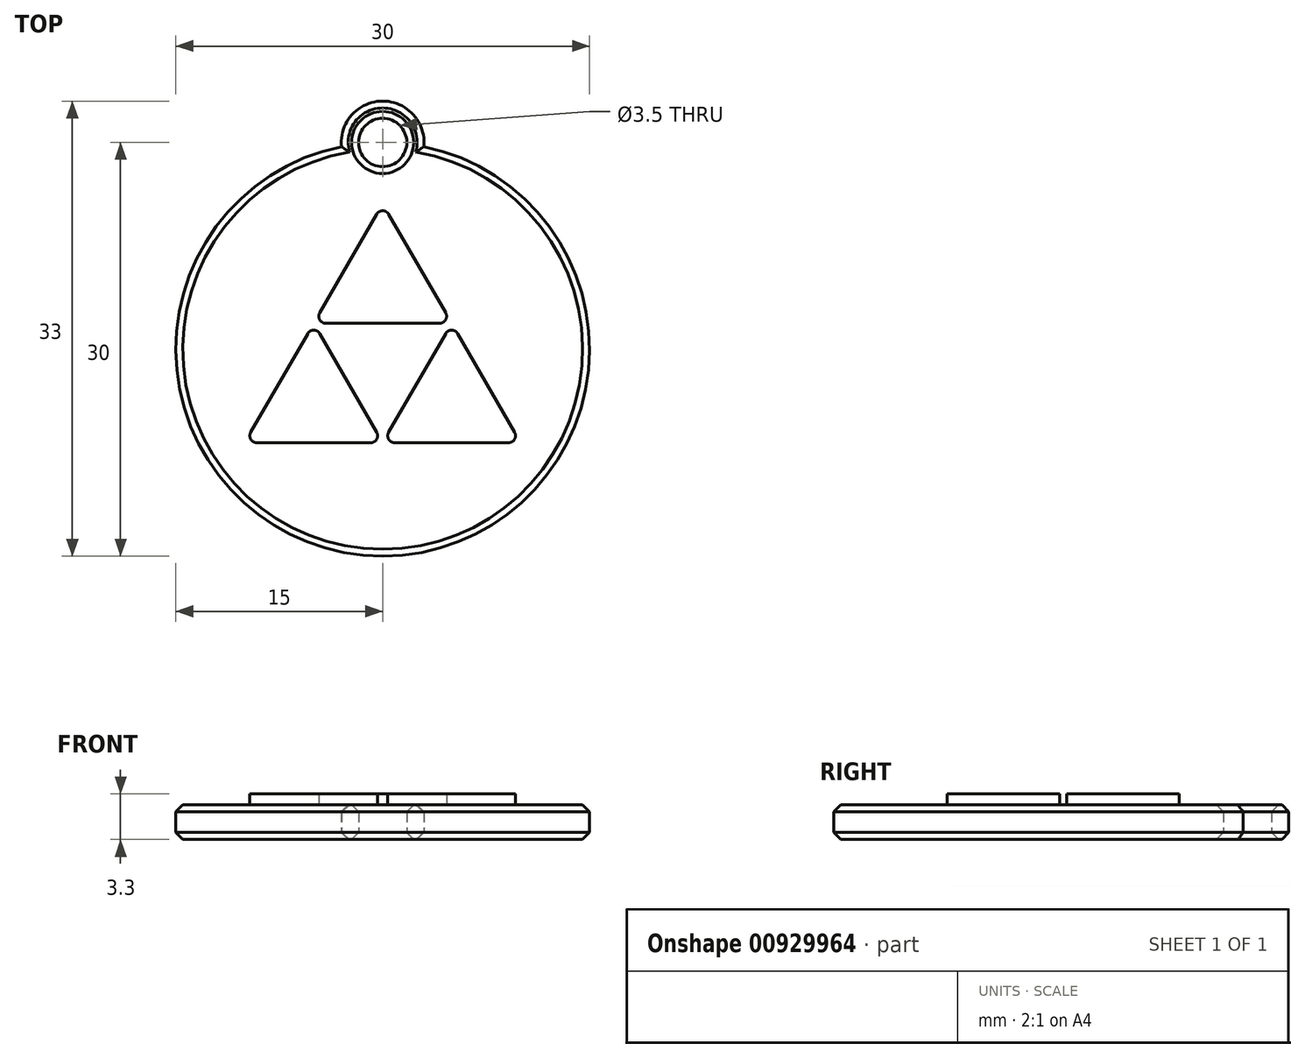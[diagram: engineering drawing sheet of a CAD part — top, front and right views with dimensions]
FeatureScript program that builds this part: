
annotation { "Feature Type Name" : "Feature", "Feature Type Description" : "" }
export const myFeature = defineFeature(function(context is Context, id is Id, definition is map)
    precondition{}
    {
        {
            var Q0;
            Q0=qCreatedBy(makeId("Top.planeOp"),FACE);
            var sketch = newSketch(context, id + "F0", { "sketchPlane" : qUnion([Q0])});
            skArc(sketch, "E0", {"start": v(-2.98, 14.7) * mm, "mid": v(0, -15) * mm, "end": v(2.98, 14.7) * mm});
            skArc(sketch, "E1", {"start": v(2.98, 14.7) * mm, "mid": v(0, 18) * mm, "end": v(-2.98, 14.7) * mm});
            skCircle(sketch, "E2", {"center": v(0, 15) * mm, "radius": 1.75 * mm});
            skSolve(sketch);
        }
        {
            var Q0;
            Q0=makeQuery(id+"F0.imprint","IMPRINT",FACE,{"disambiguationData":[TD([[makeQuery(id+"F0.imprint","IMPRINT",EDGE,{"derivedFrom":sQuery(id+"F0.wireOp",EDGE,"E0")}),1.0]])]});
            extrude(context, id + "F1", {"entities" : qUnion([Q0]), "depth" : 2.5 * mm, "offsetDistance" : 25 * mm});
        }
        {
            var Q0;
            Q0=makeQuery(id+"F1.opExtrude","CAP_FACE",FACE,{"disambiguationData":[OSD([sQuery(id+"F0.wireOp",EDGE,"E0"),sQuery(id+"F0.wireOp",EDGE,"E1"),sQuery(id+"F0.wireOp",EDGE,"E2")])],"isStart":false});
            var sketch = newSketch(context, id + "F2", { "sketchPlane" : qUnion([Q0])});
            skLineSegment(sketch, "E3", {"start": v(4.13, 1.89) * mm, "end": v(-4.13, 1.89) * mm});
            skLineSegment(sketch, "E4", {"start": v(-4.57, 2.64) * mm, "end": v(-0.43, 9.8) * mm});
            skLineSegment(sketch, "E5", {"start": v(0.43, 9.8) * mm, "end": v(4.57, 2.64) * mm});
            skLineSegment(sketch, "E6", {"start": v(-5.43, 1.14) * mm, "end": v(-9.57, -6.02) * mm});
            skLineSegment(sketch, "E7", {"start": v(-9.13, -6.77) * mm, "end": v(-0.87, -6.77) * mm});
            skLineSegment(sketch, "E8", {"start": v(-0.43, -6.02) * mm, "end": v(-4.57, 1.14) * mm});
            skLineSegment(sketch, "E9", {"start": v(0.43, -6.02) * mm, "end": v(4.57, 1.14) * mm});
            skLineSegment(sketch, "E10", {"start": v(5.43, 1.14) * mm, "end": v(9.57, -6.02) * mm});
            skLineSegment(sketch, "E11", {"start": v(9.13, -6.77) * mm, "end": v(0.87, -6.77) * mm});
            skLineSegment(sketch, "E12", {"start": v(5, 1.89) * mm, "end": v(-2.5, -2.44) * mm, "construction": true});
            skLineSegment(sketch, "E13", {"start": v(2.5, -2.44) * mm, "end": v(-5, 1.89) * mm, "construction": true});
            skPoint(sketch, "E14.visualSharp", {"position": v(0, 10.55) * mm});
            skArc(sketch, "E14.filletArc", {"start": v(0.43, 9.8) * mm, "mid": v(0, 10.05) * mm, "end": v(-0.43, 9.8) * mm});
            skPoint(sketch, "E15.visualSharp", {"position": v(-5, 1.89) * mm});
            skArc(sketch, "E15.filletArc", {"start": v(-4.57, 2.64) * mm, "mid": v(-4.57, 2.14) * mm, "end": v(-4.13, 1.89) * mm});
            skPoint(sketch, "E16.visualSharp", {"position": v(5, 1.89) * mm});
            skArc(sketch, "E16.filletArc", {"start": v(4.13, 1.89) * mm, "mid": v(4.57, 2.14) * mm, "end": v(4.57, 2.64) * mm});
            skArc(sketch, "E17.filletArc", {"start": v(5.43, 1.14) * mm, "mid": v(5, 1.39) * mm, "end": v(4.57, 1.14) * mm});
            skPoint(sketch, "E18.visualSharp", {"position": v(10, -6.77) * mm});
            skArc(sketch, "E18.filletArc", {"start": v(9.13, -6.77) * mm, "mid": v(9.57, -6.52) * mm, "end": v(9.57, -6.02) * mm});
            skPoint(sketch, "E19.visualSharp", {"position": v(0, -6.77) * mm});
            skArc(sketch, "E19.filletArc", {"start": v(0.43, -6.02) * mm, "mid": v(0.43, -6.52) * mm, "end": v(0.87, -6.77) * mm});
            skArc(sketch, "E20.filletArc", {"start": v(-0.87, -6.77) * mm, "mid": v(-0.43, -6.52) * mm, "end": v(-0.43, -6.02) * mm});
            skPoint(sketch, "E21.visualSharp", {"position": v(-10, -6.77) * mm});
            skArc(sketch, "E21.filletArc", {"start": v(-9.57, -6.02) * mm, "mid": v(-9.57, -6.52) * mm, "end": v(-9.13, -6.77) * mm});
            skArc(sketch, "E22.filletArc", {"start": v(-4.57, 1.14) * mm, "mid": v(-5, 1.39) * mm, "end": v(-5.43, 1.14) * mm});
            skPoint(sketch, "E23", {"position": v(0, -1) * mm});
            skSolve(sketch);
        }
        {
            var Q0;
            Q0=makeQuery(id+"F2.imprint","IMPRINT",FACE,{"disambiguationData":[TD([[makeQuery(id+"F2.imprint","IMPRINT",EDGE,{"derivedFrom":sQuery(id+"F2.wireOp",EDGE,"E3")}),-1.0]])]});
            var Q1;
            Q1=makeQuery(id+"F2.imprint","IMPRINT",FACE,{"disambiguationData":[TD([[makeQuery(id+"F2.imprint","IMPRINT",EDGE,{"derivedFrom":sQuery(id+"F2.wireOp",EDGE,"E6")}),1.0]])]});
            var Q2;
            Q2=makeQuery(id+"F2.imprint","IMPRINT",FACE,{"disambiguationData":[TD([[makeQuery(id+"F2.imprint","IMPRINT",EDGE,{"derivedFrom":sQuery(id+"F2.wireOp",EDGE,"E9")}),-1.0]])]});
            extrude(context, id + "F3", {"entities" : qUnion([Q0, Q1, Q2]), "operationType" : NewBodyOperationType.ADD, "depth" : .8 * mm, "offsetDistance" : 25 * mm});
        }
        {
            var Q0;
            Q0=makeQuery(id+"F1.opExtrude","CAP_EDGE",EDGE,{"disambiguationData":[OSD([sQuery(id+"F0.wireOp",EDGE,"E0")])],"isStart":false});
            var Q1;
            Q1=makeQuery(id+"F1.opExtrude","CAP_EDGE",EDGE,{"disambiguationData":[OSD([sQuery(id+"F0.wireOp",EDGE,"E0")])],"isStart":true});
            var Q2;
            Q2=makeQuery(id+"F1.opExtrude","CAP_EDGE",EDGE,{"disambiguationData":[OSD([sQuery(id+"F0.wireOp",EDGE,"E1")])],"isStart":false});
            var Q3;
            Q3=makeQuery(id+"F1.opExtrude","CAP_EDGE",EDGE,{"disambiguationData":[OSD([sQuery(id+"F0.wireOp",EDGE,"E1")])],"isStart":true});
            var Q4;
            Q4=makeQuery(id+"F1.opExtrude","CAP_EDGE",EDGE,{"disambiguationData":[OSD([sQuery(id+"F0.wireOp",EDGE,"E2")])],"isStart":true});
            var Q5;
            Q5=makeQuery(id+"F1.opExtrude","CAP_EDGE",EDGE,{"disambiguationData":[OSD([sQuery(id+"F0.wireOp",EDGE,"E2")])],"isStart":false});
            chamfer(context, id + "F4", {"entities" : qUnion([Q0, Q1, Q2, Q3, Q4, Q5]), "width" : .5 * mm, "tangentPropagation" : true});
        }
    });
